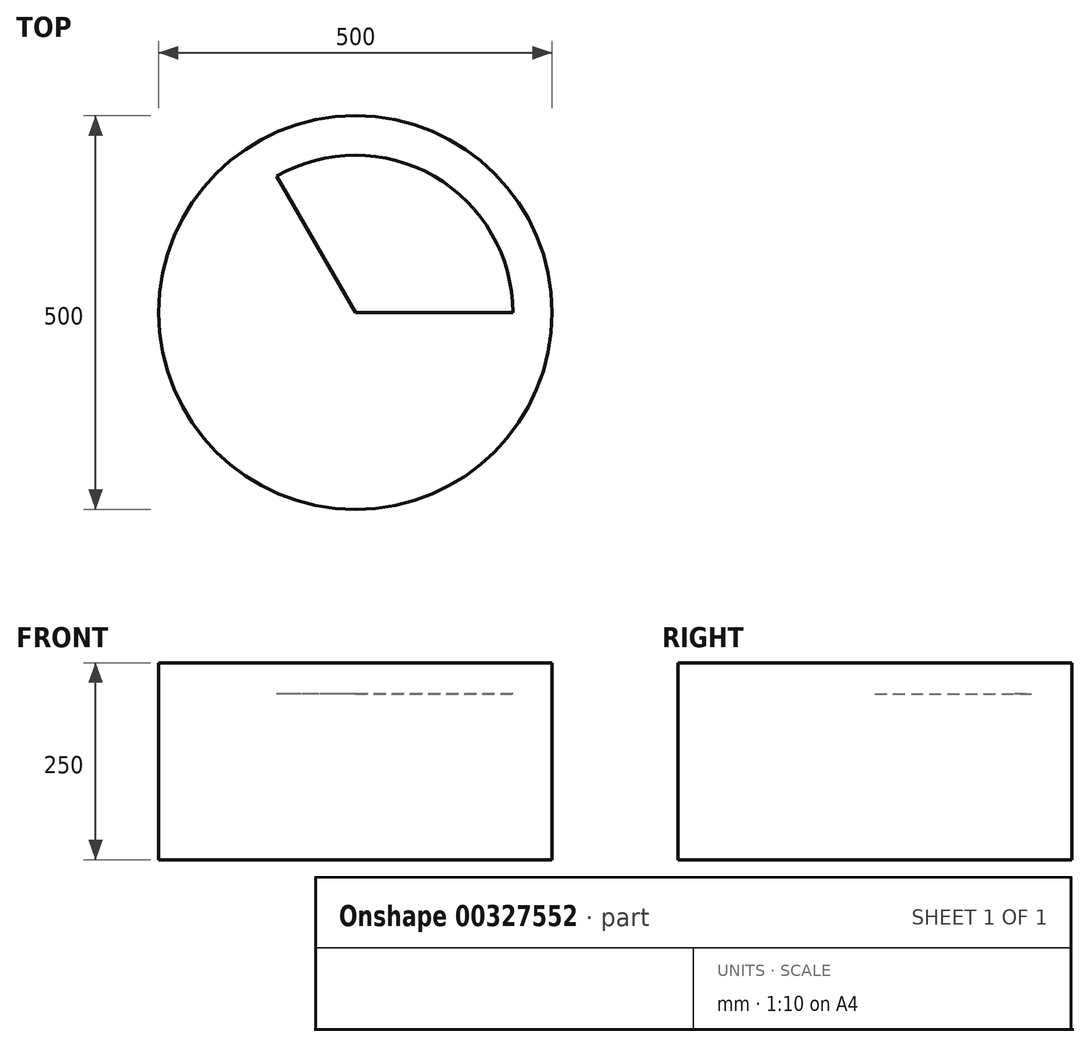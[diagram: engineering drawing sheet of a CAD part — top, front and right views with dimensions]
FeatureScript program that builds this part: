
annotation { "Feature Type Name" : "Feature", "Feature Type Description" : "" }
export const myFeature = defineFeature(function(context is Context, id is Id, definition is map)
    precondition{}
    {
        {
            var Q0;
            Q0=qCreatedBy(makeId("Front.planeOp"),FACE);
            var sketch = newSketch(context, id + "F0", { "sketchPlane" : qUnion([Q0])});
            skLineSegment(sketch, "E0", {"start": v(-250, 250) * mm, "end": v(-250, 0) * mm});
            skLineSegment(sketch, "E1", {"start": v(-250, 0) * mm, "end": v(0, 0) * mm});
            skSolve(sketch);
        }
        {
            var Q0;
            Q0=qCreatedBy(makeId("Front.planeOp"),FACE);
            var sketch = newSketch(context, id + "F1", { "sketchPlane" : qUnion([Q0])});
            skLineSegment(sketch, "E2", {"start": v(0, 0) * mm, "end": v(0, 191.44) * mm, "construction": true});
            skSolve(sketch);
        }
        {
            var Q0;
            Q0 = qConstructionFilter(qBodyType(qCreatedBy(id + "F0" ,EDGE), BodyType.WIRE), ConstructionObject.NO);
            var Q1;
            Q1=sQuery(id+"F1.wireOp",EDGE,"E2");
            revolve(context, id + "F2", {"bodyType" : ToolBodyType.SURFACE, "surfaceEntities" : qUnion([Q0]), "axis" : qUnion([Q1]), "revolveType" : RevolveType.FULL});
        }
        {
            var Q0;
            Q0=qCreatedBy(makeId("Front.planeOp"),FACE);
            var sketch = newSketch(context, id + "F3", { "sketchPlane" : qUnion([Q0])});
            skLineSegment(sketch, "E3", {"start": v(0, 210.55) * mm, "end": v(200, 210.55) * mm});
            skSolve(sketch);
        }
        {
            var Q0;
            Q0 = qConstructionFilter(qBodyType(qCreatedBy(id + "F3" ,EDGE), BodyType.WIRE), ConstructionObject.NO);
            var Q1;
            Q1=sQuery(id+"F1.wireOp",EDGE,"E2");
            revolve(context, id + "F4", {"bodyType" : ToolBodyType.SURFACE, "surfaceEntities" : qUnion([Q0]), "axis" : qUnion([Q1]), "revolveType" : RevolveType.ONE_DIRECTION, "angle" : 120 * degree});
        }
    });
